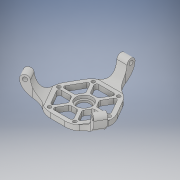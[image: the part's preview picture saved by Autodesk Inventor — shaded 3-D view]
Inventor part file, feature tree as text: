
AUTODESK INVENTOR PART (.ipt)
format: ipt  version: 2019.4 (Build 234330000, 330)  size: 382,976 bytes
history: native  units: mm
features: extrude x6, sketch x6, fillet x4, pattern_circular x3, plane x2
ambient origin geometry x8: Origin, YZ Plane, XZ Plane, XY Plane, X Axis, Y Axis, Z Axis, Center Point
bodies: Solid1 (feature_tree)
feature tree (21):
  extrude  "Extrusion1"  Depth=25.980762mm
  plane  "Work Plane2"
  extrude  "Extrusion3"  Depth=5.0mm TaperAngle=30.0deg
  fillet  "Fillet1"  Radius=15.5mm
  extrude  "Extrusion4"  Depth=20.0mm
  pattern_circular  "Circular Pattern1"  [2 undecoded]
  fillet  "Fillet2"  Radius=10.0mm
  extrude  "Extrusion5"  Depth=3.0mm
  pattern_circular  "Circular Pattern2"  [2 undecoded]
  fillet  "Fillet3"  Radius=30.0mm
  pattern_circular  "Circular Pattern3"  [2 undecoded]
  fillet  "Fillet4"  Radius=4.0mm
  extrude  "Extrusion6"  TaperAngle=30.0deg  [1 undecoded]
  extrude  "Extrusion7"  Depth=3.0mm
  sketch  "Sketch1"  dims[d0=30.0mm d1=25.980762mm]
  plane  "Work Plane1"
  sketch  "Sketch4"  dims[d2=5.0mm d3=0.0mm d7=30.0deg d14=15.0mm d15=15.5mm]
  sketch  "Sketch5"  dims[d16=90.0deg d17=20.0mm]
  sketch  "Sketch6"  dims[d18=90.0deg]
  sketch  "Sketch7"  dims[d19=4.0mm]
  sketch  "Sketch10"  dims[d20=8.0mm d21=10.0mm d22=0.0mm d23=10.0mm d24=12.0mm d25=10.0mm d26=0.0mm d27=30.0mm d28=360.0deg d30=10.0mm d31=4.0mm d32=30.0deg d33=11.0mm d34=60.0deg d35=11.0mm d36=120.0deg d37=12.0mm d38=30.0deg d39=4.0mm d40=4.0mm d41=10.0mm d42=0.0mm d43=60.0mm d44=360.0deg d46=2.0mm d47=60.0mm d48=360.0deg d50=20.0mm d51=25.0mm d52=3.5mm d53=60.0mm d55=360.0deg d57=10.0mm d58=0.0mm d59=16.0mm d60=3.0mm d61=0.0mm]
note: 7 required parameter values undecoded (feature->parameter linkage not recoverable at this tier; creation-order binding heuristic only, values carry confidence <= 0.55)
